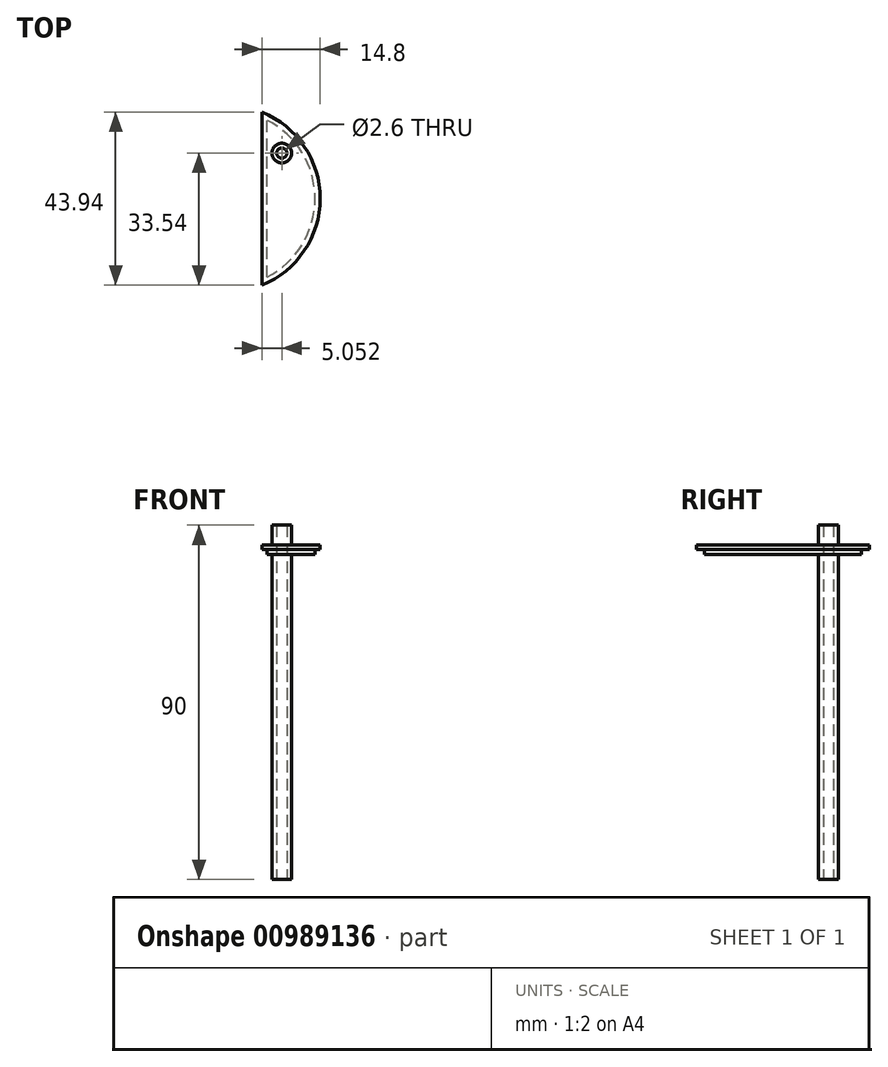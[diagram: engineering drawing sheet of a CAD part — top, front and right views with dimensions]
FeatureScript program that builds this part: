
annotation { "Feature Type Name" : "Feature", "Feature Type Description" : "" }
export const myFeature = defineFeature(function(context is Context, id is Id, definition is map)
    precondition{}
    {
        {
            var Q0;
            Q0=qCreatedBy(makeId("Top.planeOp"),FACE);
            var sketch = newSketch(context, id + "F0", { "sketchPlane" : qUnion([Q0])});
            skArc(sketch, "E0", {"start": v(10.2, -19.94) * mm, "mid": v(22.4, 0) * mm, "end": v(10.2, 19.94) * mm});
            skLineSegment(sketch, "E1", {"start": v(10.2, -19.94) * mm, "end": v(10.2, 19.94) * mm});
            skCircle(sketch, "E2", {"center": v(13.95, 11.57) * mm, "radius": 2.5 * mm});
            skCircle(sketch, "E3", {"center": v(13.95, 11.57) * mm, "radius": 1.3 * mm});
            skArc(sketch, "E4", {"start": v(8.9, -21.97) * mm, "mid": v(23.7, 0) * mm, "end": v(8.9, 21.97) * mm});
            skLineSegment(sketch, "E5", {"start": v(8.9, 21.97) * mm, "end": v(8.9, -21.97) * mm});
            skSolve(sketch);
        }
        {
            var Q0;
            Q0=makeQuery(id+"F0.imprint","IMPRINT",FACE,{"disambiguationData":[TD([[makeQuery(id+"F0.imprint","IMPRINT",EDGE,{"derivedFrom":sQuery(id+"F0.wireOp",EDGE,"E0")}),1.0]])]});
            var Q1;
            Q1=makeQuery(id+"F0.imprint","IMPRINT",FACE,{"disambiguationData":[TD([[makeQuery(id+"F0.imprint","IMPRINT",EDGE,{"derivedFrom":sQuery(id+"F0.wireOp",EDGE,"E0")}),-1.0]])]});
            extrude(context, id + "F1", {"entities" : qUnion([Q0, Q1]), "depth" : 2.5 * mm, "offsetDistance" : 25.4 * mm});
        }
        {
            var Q0;
            Q0=makeQuery(id+"F0.imprint","IMPRINT",FACE,{"disambiguationData":[TD([[makeQuery(id+"F0.imprint","IMPRINT",EDGE,{"derivedFrom":sQuery(id+"F0.wireOp",EDGE,"E2")}),1.0]])]});
            extrude(context, id + "F2", {"entities" : qUnion([Q0]), "operationType" : NewBodyOperationType.ADD, "depth" : 7.5 * mm, "offsetDistance" : 25.4 * mm});
        }
        {
            var Q0;
            Q0=makeQuery(id+"F2.opExtrude","CAP_FACE",FACE,{"disambiguationData":[OSD([sQuery(id+"F0.wireOp",EDGE,"E2"),sQuery(id+"F0.wireOp",EDGE,"E3")])],"isStart":false});
            extrude(context, id + "F3", {"entities" : qUnion([Q0]), "operationType" : NewBodyOperationType.ADD, "oppositeDirection" : true, "depth" : 90 * mm, "offsetDistance" : 25.4 * mm});
        }
        {
            var Q0;
            Q0=makeQuery(id+"F0.imprint","IMPRINT",FACE,{"disambiguationData":[TD([[makeQuery(id+"F0.imprint","IMPRINT",EDGE,{"derivedFrom":sQuery(id+"F0.wireOp",EDGE,"E0")}),-1.0]])]});
            extrude(context, id + "F4", {"entities" : qUnion([Q0]), "operationType" : NewBodyOperationType.REMOVE, "depth" : 1.3 * mm, "offsetDistance" : 25.4 * mm});
        }
    });
